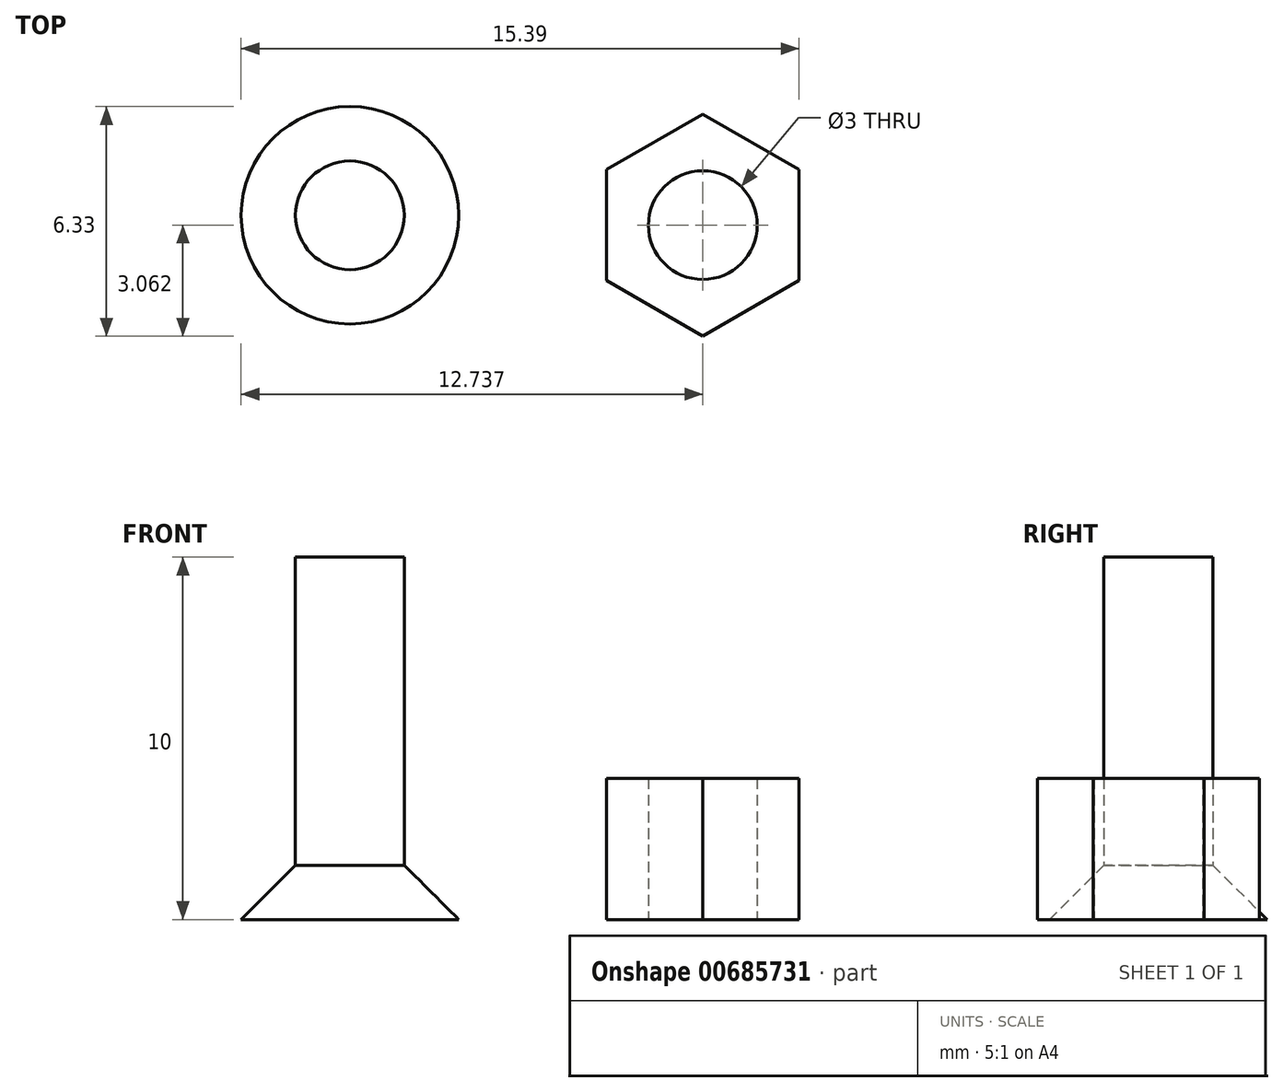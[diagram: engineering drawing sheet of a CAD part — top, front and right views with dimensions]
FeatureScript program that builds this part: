
annotation { "Feature Type Name" : "Feature", "Feature Type Description" : "" }
export const myFeature = defineFeature(function(context is Context, id is Id, definition is map)
    precondition{}
    {
        {
            var Q0;
            Q0=qCreatedBy(makeId("Top.planeOp"),FACE);
            var sketch = newSketch(context, id + "F0", { "sketchPlane" : qUnion([Q0])});
            skCircle(sketch, "E0", {"center": v(-21.6, 27.34) * mm, "radius": 3 * mm});
            skCircle(sketch, "E1", {"center": v(-21.6, 27.34) * mm, "radius": 1.5 * mm});
            skCircle(sketch, "E2.cCircle", {"center": v(-11.87, 27.07) * mm, "radius": 2.65 * mm, "construction": true});
            skLineSegment(sketch, "E2.0", {"start": v(-9.22, 28.6) * mm, "end": v(-9.22, 25.54) * mm});
            skLineSegment(sketch, "E2.1", {"start": v(-9.22, 25.54) * mm, "end": v(-11.87, 24.01) * mm});
            skLineSegment(sketch, "E2.2", {"start": v(-11.87, 24.01) * mm, "end": v(-14.52, 25.54) * mm});
            skLineSegment(sketch, "E2.3", {"start": v(-14.52, 25.54) * mm, "end": v(-14.52, 28.6) * mm});
            skLineSegment(sketch, "E2.4", {"start": v(-14.52, 28.6) * mm, "end": v(-11.87, 30.13) * mm});
            skLineSegment(sketch, "E2.5", {"start": v(-11.87, 30.13) * mm, "end": v(-9.22, 28.6) * mm});
            skPoint(sketch, "E2.0.midPoint", {"position": v(-9.22, 27.07) * mm});
            skCircle(sketch, "E3", {"center": v(-11.87, 27.07) * mm, "radius": 1.5 * mm});
            skSolve(sketch);
        }
        {
            var Q0;
            Q0=makeQuery(id+"F0.imprint","IMPRINT",FACE,{"disambiguationData":[TD([[makeQuery(id+"F0.imprint","IMPRINT",EDGE,{"derivedFrom":sQuery(id+"F0.wireOp",EDGE,"E1")}),1.0]])]});
            extrude(context, id + "F1", {"entities" : qUnion([Q0]), "depth" : 10 * mm, "offsetDistance" : 25 * mm});
        }
        {
            var Q0;
            Q0=makeQuery(id+"F0.imprint","IMPRINT",FACE,{"disambiguationData":[TD([[makeQuery(id+"F0.imprint","IMPRINT",EDGE,{"derivedFrom":sQuery(id+"F0.wireOp",EDGE,"E0")}),1.0]])]});
            extrude(context, id + "F2", {"entities" : qUnion([Q0]), "operationType" : NewBodyOperationType.ADD, "depth" : 1.5 * mm, "offsetDistance" : 25 * mm});
        }
        {
            var Q0;
            Q0=makeQuery(id+"F2.opExtrude","CAP_EDGE",EDGE,{"disambiguationData":[OSD([sQuery(id+"F0.wireOp",EDGE,"E0")])],"isStart":false});
            chamfer(context, id + "F3", {"entities" : qUnion([Q0]), "width" : 1.5 * mm, "tangentPropagation" : true});
        }
        {
            var Q0;
            Q0=makeQuery(id+"F0.imprint","IMPRINT",FACE,{"disambiguationData":[TD([[makeQuery(id+"F0.imprint","IMPRINT",EDGE,{"derivedFrom":sQuery(id+"F0.wireOp",EDGE,"E2.0")}),-1.0]])]});
            extrude(context, id + "F4", {"entities" : qUnion([Q0]), "depth" : 3.9 * mm, "offsetDistance" : 25 * mm});
        }
    });
